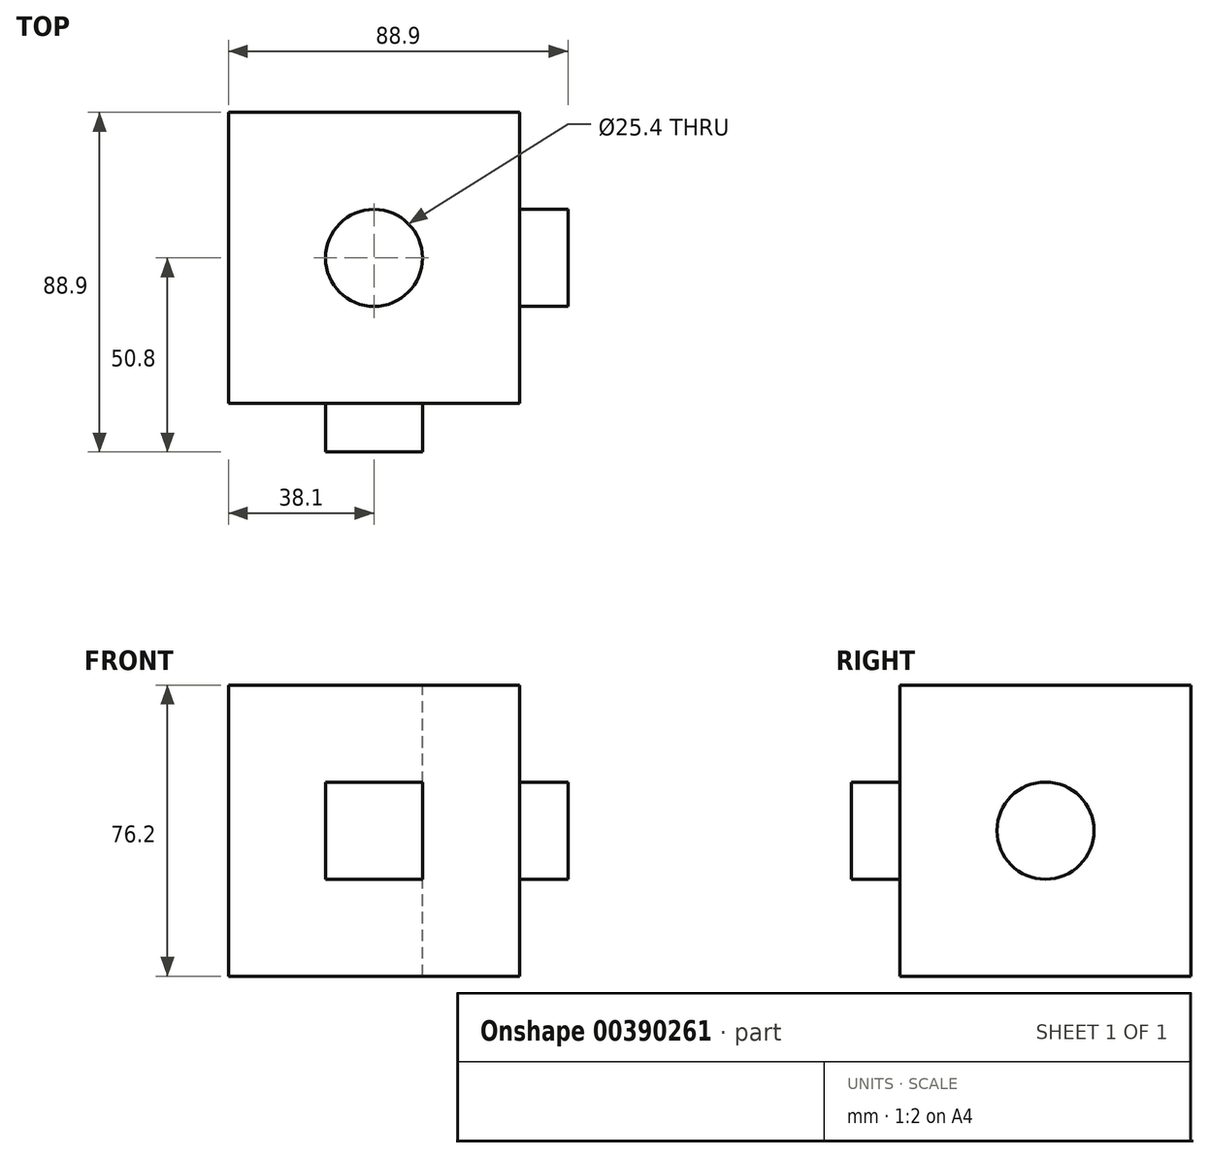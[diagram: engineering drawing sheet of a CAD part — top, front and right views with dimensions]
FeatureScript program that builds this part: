
annotation { "Feature Type Name" : "Feature", "Feature Type Description" : "" }
export const myFeature = defineFeature(function(context is Context, id is Id, definition is map)
    precondition{}
    {
        {
            var Q0;
            Q0=qCreatedBy(makeId("Front.planeOp"),FACE);
            var sketch = newSketch(context, id + "F0", { "sketchPlane" : qUnion([Q0])});
            skLineSegment(sketch, "E0.bottom", {"start": v(-38.59, 55.9) * mm, "end": v(37.61, 55.9) * mm});
            skLineSegment(sketch, "E0.top", {"start": v(-38.59, -20.3) * mm, "end": v(37.61, -20.3) * mm});
            skLineSegment(sketch, "E0.left", {"start": v(-38.59, 55.9) * mm, "end": v(-38.59, -20.3) * mm});
            skLineSegment(sketch, "E0.right", {"start": v(37.61, 55.9) * mm, "end": v(37.61, -20.3) * mm});
            skSolve(sketch);
        }
        {
            var Q0;
            Q0=makeQuery(id+"F0.imprint","IMPRINT",FACE,{"disambiguationData":[TD([[makeQuery(id+"F0.imprint","IMPRINT",EDGE,{"derivedFrom":sQuery(id+"F0.wireOp",EDGE,"E0.bottom")}),-1.0]])]});
            extrude(context, id + "F1", {"entities" : qUnion([Q0]), "depth" : 76.2 * mm});
        }
        {
            var Q0;
            Q0=makeQuery(id+"F1.opExtrude","SWEPT_FACE",FACE,{"disambiguationData":[OSD([sQuery(id+"F0.wireOp",EDGE,"E0.bottom")])]});
            var sketch = newSketch(context, id + "F2", { "sketchPlane" : qUnion([Q0])});
            skPoint(sketch, "E1", {"position": v(-0.49, -38.1) * mm});
            skSolve(sketch);
        }
        {
            var Q0;
            Q0=sQuery(id+"F2.wireOp",VERTEX,"E1");
            var Q1;
            Q1=makeQuery(id+"F1.opExtrude","SWEPT_BODY",BODY,{"disambiguationData":[OSD([sQuery(id+"F0.wireOp",EDGE,"E0.bottom"),sQuery(id+"F0.wireOp",EDGE,"E0.top"),sQuery(id+"F0.wireOp",EDGE,"E0.left"),sQuery(id+"F0.wireOp",EDGE,"E0.right")])]});
            hole(context, id + "F3", {"style" : HoleStyle.SIMPLE, "endStyle" : HoleEndStyle.THROUGH, "holeDiameter" : 25.4 * mm, "isTappedThrough" : true, "tappedDepth" : 12.7 * mm, "tapClearance" : 3, "locations" : qUnion([Q0]), "scope" : qUnion([Q1])});
        }
        {
            var Q0;
            Q0=makeQuery(id+"F1.opExtrude","CAP_FACE",FACE,{"disambiguationData":[OSD([sQuery(id+"F0.wireOp",EDGE,"E0.bottom"),sQuery(id+"F0.wireOp",EDGE,"E0.top"),sQuery(id+"F0.wireOp",EDGE,"E0.left"),sQuery(id+"F0.wireOp",EDGE,"E0.right")])],"isStart":false});
            var sketch = newSketch(context, id + "F4", { "sketchPlane" : qUnion([Q0])});
            skLineSegment(sketch, "E2.bottom", {"start": v(-13.19, 30.5) * mm, "end": v(12.21, 30.5) * mm});
            skLineSegment(sketch, "E2.top", {"start": v(-13.19, 5.1) * mm, "end": v(12.21, 5.1) * mm});
            skLineSegment(sketch, "E2.left", {"start": v(-13.19, 30.5) * mm, "end": v(-13.19, 5.1) * mm});
            skLineSegment(sketch, "E2.right", {"start": v(12.21, 30.5) * mm, "end": v(12.21, 5.1) * mm});
            skSolve(sketch);
        }
        {
            var Q0;
            Q0 = qSketchRegion(id + "F4", true);
            extrude(context, id + "F5", {"entities" : qUnion([Q0]), "operationType" : NewBodyOperationType.ADD, "depth" : 12.7 * mm});
        }
        {
            var Q0;
            Q0=makeQuery(id+"F1.opExtrude","SWEPT_FACE",FACE,{"disambiguationData":[OSD([sQuery(id+"F0.wireOp",EDGE,"E0.right")])]});
            var sketch = newSketch(context, id + "F6", { "sketchPlane" : qUnion([Q0])});
            skCircle(sketch, "E3", {"center": v(-38.1, 17.8) * mm, "radius": 12.7 * mm});
            skSolve(sketch);
        }
        {
            var Q0;
            Q0=makeQuery(id+"F6.imprint","IMPRINT",FACE,{"disambiguationData":[TD([[makeQuery(id+"F6.imprint","IMPRINT",EDGE,{"derivedFrom":sQuery(id+"F6.wireOp",EDGE,"E3")}),1.0]])]});
            extrude(context, id + "F7", {"entities" : qUnion([Q0]), "operationType" : NewBodyOperationType.ADD, "depth" : 12.7 * mm});
        }
    });
